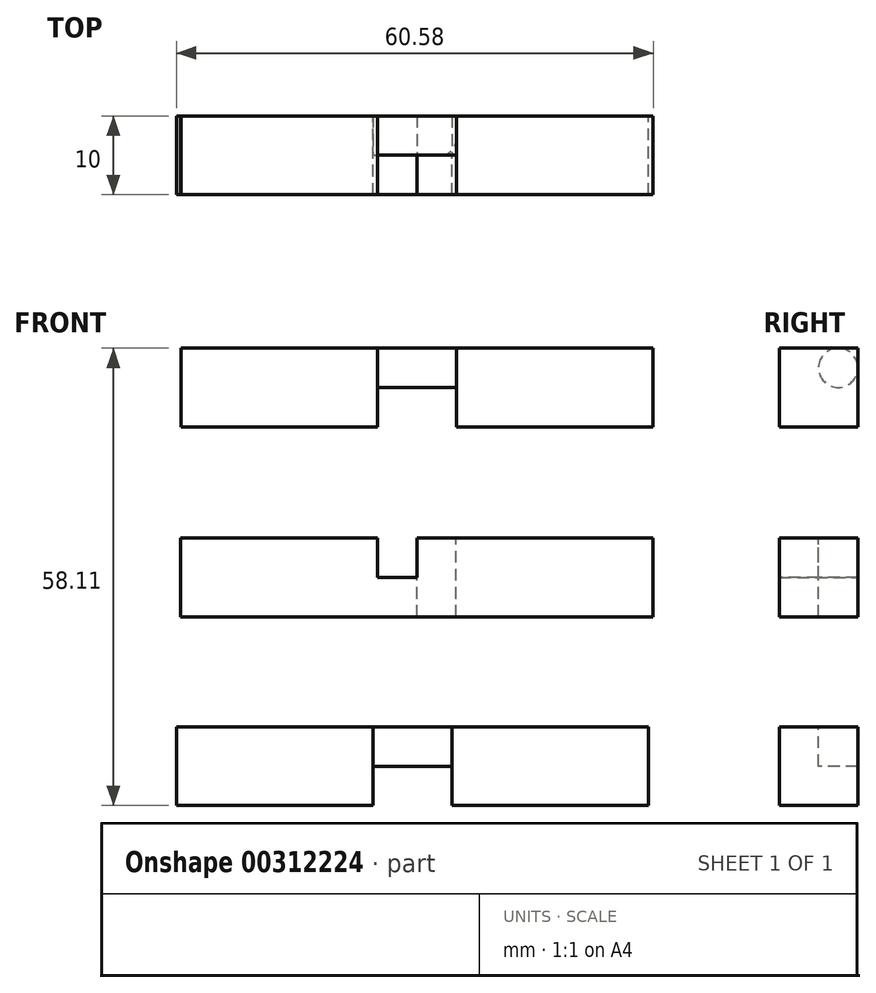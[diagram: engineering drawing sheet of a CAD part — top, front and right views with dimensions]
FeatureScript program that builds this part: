
annotation { "Feature Type Name" : "Feature", "Feature Type Description" : "" }
export const myFeature = defineFeature(function(context is Context, id is Id, definition is map)
    precondition{}
    {
        {
            var Q0;
            Q0=qCreatedBy(makeId("Front.planeOp"),FACE);
            var sketch = newSketch(context, id + "F0", { "sketchPlane" : qUnion([Q0])});
            skLineSegment(sketch, "E0.bottom", {"start": v(-46.78, 48.11) * mm, "end": v(13.22, 48.11) * mm});
            skLineSegment(sketch, "E0.top", {"start": v(-46.78, 38.11) * mm, "end": v(13.22, 38.11) * mm});
            skLineSegment(sketch, "E0.left", {"start": v(-46.78, 48.11) * mm, "end": v(-46.78, 38.11) * mm});
            skLineSegment(sketch, "E0.right", {"start": v(13.22, 48.11) * mm, "end": v(13.22, 38.11) * mm});
            skLineSegment(sketch, "E1.bottom", {"start": v(-46.81, 23.97) * mm, "end": v(13.19, 23.97) * mm});
            skLineSegment(sketch, "E1.top", {"start": v(-46.81, 13.97) * mm, "end": v(13.19, 13.97) * mm});
            skLineSegment(sketch, "E1.left", {"start": v(-46.81, 23.97) * mm, "end": v(-46.81, 13.97) * mm});
            skLineSegment(sketch, "E1.right", {"start": v(13.19, 23.97) * mm, "end": v(13.19, 13.97) * mm});
            skLineSegment(sketch, "E2.bottom", {"start": v(-47.36, 0) * mm, "end": v(12.64, 0) * mm});
            skLineSegment(sketch, "E2.top", {"start": v(-47.36, -10) * mm, "end": v(12.64, -10) * mm});
            skLineSegment(sketch, "E2.left", {"start": v(-47.36, 0) * mm, "end": v(-47.36, -10) * mm});
            skLineSegment(sketch, "E2.right", {"start": v(12.64, 0) * mm, "end": v(12.64, -10) * mm});
            skSolve(sketch);
        }
        {
            var Q0;
            Q0=makeQuery(id+"F0.imprint","IMPRINT",FACE,{"disambiguationData":[TD([[makeQuery(id+"F0.imprint","IMPRINT",EDGE,{"derivedFrom":sQuery(id+"F0.wireOp",EDGE,"E0.bottom")}),-1.0]])]});
            var Q1;
            Q1=makeQuery(id+"F0.imprint","IMPRINT",FACE,{"disambiguationData":[TD([[makeQuery(id+"F0.imprint","IMPRINT",EDGE,{"derivedFrom":sQuery(id+"F0.wireOp",EDGE,"E1.bottom")}),-1.0]])]});
            var Q2;
            Q2=makeQuery(id+"F0.imprint","IMPRINT",FACE,{"disambiguationData":[TD([[makeQuery(id+"F0.imprint","IMPRINT",EDGE,{"derivedFrom":sQuery(id+"F0.wireOp",EDGE,"E2.bottom")}),-1.0]])]});
            extrude(context, id + "F1", {"entities" : qUnion([Q0, Q1, Q2]), "depth" : 10 * mm});
        }
        {
            var Q0;
            Q0=makeQuery(id+"F1.opExtrude","SWEPT_FACE",FACE,{"disambiguationData":[OSD([sQuery(id+"F0.wireOp",EDGE,"E2.bottom")])]});
            var sketch = newSketch(context, id + "F2", { "sketchPlane" : qUnion([Q0])});
            skLineSegment(sketch, "E3", {"start": v(-47.36, -10) * mm, "end": v(-27.36, -10) * mm});
            skLineSegment(sketch, "E4", {"start": v(12.64, -10) * mm, "end": v(-17.36, -10) * mm});
            skLineSegment(sketch, "E5", {"start": v(-47.36, -10) * mm, "end": v(-22.36, -10) * mm});
            skLineSegment(sketch, "E6", {"start": v(12.64, -10) * mm, "end": v(-12.36, -10) * mm});
            skLineSegment(sketch, "E7", {"start": v(-22.36, -10) * mm, "end": v(-22.36, -5) * mm});
            skLineSegment(sketch, "E8", {"start": v(-12.36, -10) * mm, "end": v(-12.36, -5) * mm});
            skLineSegment(sketch, "E9", {"start": v(-22.36, -5) * mm, "end": v(-12.36, -5) * mm});
            skSolve(sketch);
        }
        {
            var Q0;
            {var subQ1=sQuery(id+"F2.wireOp",EDGE,"E4");Q0=makeQuery(id+"F2.imprint","IMPRINT",FACE,{"disambiguationData":[TD([[makeQuery(id+"F2.imprint","IMPRINT",EDGE,{"derivedFrom":subQ1}),1.0]])]});}
            extrude(context, id + "F3", {"entities" : qUnion([Q0]), "operationType" : NewBodyOperationType.REMOVE, "oppositeDirection" : true, "depth" : 10 * mm});
        }
        {
            var Q0;
            Q0=makeQuery(id+"F3.boolean.opBoolean","COPY",FACE,{"derivedFrom":makeQuery(id+"F3.opExtrude","SWEPT_FACE",FACE,{"disambiguationData":[OSD([sQuery(id+"F2.wireOp",EDGE,"E9")])]})});
            var sketch = newSketch(context, id + "F4", { "sketchPlane" : qUnion([Q0])});
            skLineSegment(sketch, "E10", {"start": v(-22.36, -10) * mm, "end": v(-22.36, -5) * mm});
            skLineSegment(sketch, "E11", {"start": v(-12.36, -10) * mm, "end": v(-12.36, -5) * mm});
            skLineSegment(sketch, "E12", {"start": v(-22.36, -5) * mm, "end": v(-12.36, -5) * mm});
            skSolve(sketch);
        }
        {
            var Q0;
            Q0=makeQuery(id+"F4.imprint","IMPRINT",FACE,{"disambiguationData":[TD([[makeQuery(id+"F4.imprint","IMPRINT",EDGE,{"derivedFrom":sQuery(id+"F4.wireOp",EDGE,"E10")}),-1.0]])]});
            extrude(context, id + "F5", {"entities" : qUnion([Q0]), "operationType" : NewBodyOperationType.REMOVE, "oppositeDirection" : true, "depth" : 5 * mm});
        }
        {
            var Q0;
            Q0=makeQuery(id+"F1.opExtrude","SWEPT_FACE",FACE,{"disambiguationData":[OSD([sQuery(id+"F0.wireOp",EDGE,"E1.bottom")])]});
            var sketch = newSketch(context, id + "F6", { "sketchPlane" : qUnion([Q0])});
            skLineSegment(sketch, "E13", {"start": v(-46.81, -10) * mm, "end": v(-21.81, -10) * mm});
            skLineSegment(sketch, "E14", {"start": v(13.19, -10) * mm, "end": v(-11.81, -10) * mm});
            skLineSegment(sketch, "E15", {"start": v(-21.81, -10) * mm, "end": v(-21.81, 0) * mm});
            skLineSegment(sketch, "E16", {"start": v(-21.81, 0) * mm, "end": v(-16.81, 0) * mm});
            skLineSegment(sketch, "E17", {"start": v(-16.81, 0) * mm, "end": v(-16.81, -10) * mm});
            skLineSegment(sketch, "E18", {"start": v(-16.81, -10) * mm, "end": v(-16.81, -5) * mm});
            skLineSegment(sketch, "E19", {"start": v(-16.81, -5) * mm, "end": v(-11.81, -5) * mm});
            skLineSegment(sketch, "E20", {"start": v(-11.81, -5) * mm, "end": v(-11.81, 0) * mm});
            skSolve(sketch);
        }
        {
            var Q0;
            {var subQ6=sQuery(id+"F6.wireOp",EDGE,"E15");Q0=makeQuery(id+"F6.imprint","IMPRINT",FACE,{"disambiguationData":[TD([[makeQuery(id+"F6.imprint","IMPRINT",EDGE,{"derivedFrom":subQ6}),-1.0]])]});}
            extrude(context, id + "F7", {"entities" : qUnion([Q0]), "operationType" : NewBodyOperationType.REMOVE, "oppositeDirection" : true, "depth" : 5 * mm});
        }
        {
            var Q0;
            {var subQ0=sQuery(id+"F6.wireOp",EDGE,"E17");Q0=makeQuery(id+"F6.imprint","IMPRINT",FACE,{"disambiguationData":[TD([[makeQuery(id+"F6.imprint","IMPRINT",EDGE,{"derivedFrom":subQ0}),1.0]])]});}
            extrude(context, id + "F8", {"entities" : qUnion([Q0]), "operationType" : NewBodyOperationType.REMOVE, "oppositeDirection" : true, "depth" : 10 * mm});
        }
        {
            var Q0;
            Q0=makeQuery(id+"F8.boolean.opBoolean","COPY",EDGE,{"derivedFrom":makeQuery(id+"F8.opExtrude","SWEPT_EDGE",EDGE,{"disambiguationData":[OSD([sQuery(id+"F6.wireOp",EDGE,"E19"),sQuery(id+"F6.wireOp",EDGE,"E20")])]})});
            fillet(context, id + "F9", {"entities" : qUnion([Q0]), "radius" : 2 * mm, "tangentPropagation" : true, "allowEdgeOverflow" : false});
        }
        {
            var Q0;
            Q0=makeQuery(id+"F1.opExtrude","SWEPT_FACE",FACE,{"disambiguationData":[OSD([sQuery(id+"F0.wireOp",EDGE,"E0.left")])]});
            var sketch = newSketch(context, id + "F10", { "sketchPlane" : qUnion([Q0])});
            skLineSegment(sketch, "E21", {"start": v(10, 48.11) * mm, "end": v(5, 48.11) * mm});
            skLineSegment(sketch, "E22", {"start": v(5, 48.11) * mm, "end": v(5, 43.11) * mm});
            skLineSegment(sketch, "E23", {"start": v(5, 43.11) * mm, "end": v(0, 43.11) * mm});
            skLineSegment(sketch, "E24", {"start": v(0, 43.11) * mm, "end": v(0, 45.61) * mm});
            skLineSegment(sketch, "E25", {"start": v(0, 45.61) * mm, "end": v(2.5, 45.61) * mm});
            skCircle(sketch, "E26", {"center": v(2.5, 45.61) * mm, "radius": 2.5 * mm});
            skSolve(sketch);
        }
        {
            var Q0;
            {var subQ0=sQuery(id+"F10.wireOp",EDGE,"E26");var subQ1=sQuery(id+"F0.wireOp",EDGE,"E0.left");var subQ2=makeQuery(id+"F1.opExtrude","CAP_EDGE",EDGE,{"disambiguationData":[OSD([subQ1])],"isStart":true});var subQ3=makeQuery(id+"F10.imprint","INTERSECT",VERTEX,{"derivedFrom":[subQ2,sQuery(id+"F10.wireOp",EDGE,"E24"),subQ0]});Q0=makeQuery(id+"F10.imprint","IMPRINT",FACE,{"disambiguationData":[TD([[makeQuery(id+"F10.imprint","IMPRINT",EDGE,{"disambiguationData":[TD([[subQ3,1.0]])],"derivedFrom":subQ0}),-1.0]])]});}
            var Q1;
            {var subQ0=sQuery(id+"F10.wireOp",EDGE,"E22");var subQ3=sQuery(id+"F10.wireOp",EDGE,"E26");var subQ4=makeQuery(id+"F10.imprint","INTERSECT",VERTEX,{"derivedFrom":[subQ0,subQ3]});Q1=makeQuery(id+"F10.imprint","IMPRINT",FACE,{"disambiguationData":[TD([[makeQuery(id+"F10.imprint","IMPRINT",EDGE,{"disambiguationData":[TD([[subQ4,-1.0]])],"derivedFrom":subQ3}),-1.0]])]});}
            var Q2;
            {var subQ0=sQuery(id+"F10.wireOp",EDGE,"E24");Q2=makeQuery(id+"F10.imprint","IMPRINT",FACE,{"disambiguationData":[TD([[makeQuery(id+"F10.imprint","IMPRINT",EDGE,{"derivedFrom":subQ0}),1.0]])]});}
            var Q3;
            {var subQ0=sQuery(id+"F10.wireOp",EDGE,"E23");var subQ1=sQuery(id+"F10.wireOp",EDGE,"E22");var subQ2=makeQuery(id+"F10.imprint","INTERSECT",VERTEX,{"derivedFrom":[subQ1,subQ0]});Q3=makeQuery(id+"F10.imprint","IMPRINT",FACE,{"disambiguationData":[TD([[makeQuery(id+"F10.imprint","IMPRINT",EDGE,{"disambiguationData":[TD([[subQ2,1.0]])],"derivedFrom":subQ1}),-1.0]])]});}
            var Q4;
            {var subQ6=sQuery(id+"F10.wireOp",EDGE,"E21");Q4=makeQuery(id+"F10.imprint","IMPRINT",FACE,{"disambiguationData":[TD([[makeQuery(id+"F10.imprint","IMPRINT",EDGE,{"derivedFrom":subQ6}),1.0]])]});}
            extrude(context, id + "F11", {"entities" : qUnion([Q0, Q1, Q2, Q3, Q4]), "operationType" : NewBodyOperationType.REMOVE, "oppositeDirection" : true, "depth" : 35 * mm});
        }
        {
            var Q0;
            Q0=makeQuery(id+"F1.opExtrude","SWEPT_FACE",FACE,{"disambiguationData":[OSD([sQuery(id+"F0.wireOp",EDGE,"E0.left")])]});
            extrude(context, id + "F12", {"entities" : qUnion([Q0]), "operationType" : NewBodyOperationType.REMOVE, "oppositeDirection" : true, "depth" : 25 * mm});
        }
        {
            var Q0;
            Q0=makeQuery(id+"F12.boolean.opBoolean","COPY",FACE,{"derivedFrom":makeQuery(id+"F12.opExtrude","CAP_FACE",FACE,{"disambiguationData":[OSD([sQuery(id+"F0.wireOp",EDGE,"E0.left")])],"isStart":false})});
            var sketch = newSketch(context, id + "F13", { "sketchPlane" : qUnion([Q0])});
            skLineSegment(sketch, "E27", {"start": v(2.5, 45.61) * mm, "end": v(2.5, 48.11) * mm});
            skLineSegment(sketch, "E28", {"start": v(2.5, 48.11) * mm, "end": v(0, 48.11) * mm});
            skLineSegment(sketch, "E29", {"start": v(0, 48.11) * mm, "end": v(0, 38.11) * mm});
            skLineSegment(sketch, "E30", {"start": v(0, 38.11) * mm, "end": v(10, 38.11) * mm});
            skLineSegment(sketch, "E31", {"start": v(10, 38.11) * mm, "end": v(10, 48.11) * mm});
            skLineSegment(sketch, "E32", {"start": v(2.5, 48.11) * mm, "end": v(10, 48.11) * mm});
            skSolve(sketch);
        }
        {
            var Q0;
            Q0 = qSketchRegion(id + "F13", true);
            extrude(context, id + "F14", {"entities" : qUnion([Q0]), "operationType" : NewBodyOperationType.ADD, "depth" : 25 * mm});
        }
    });
